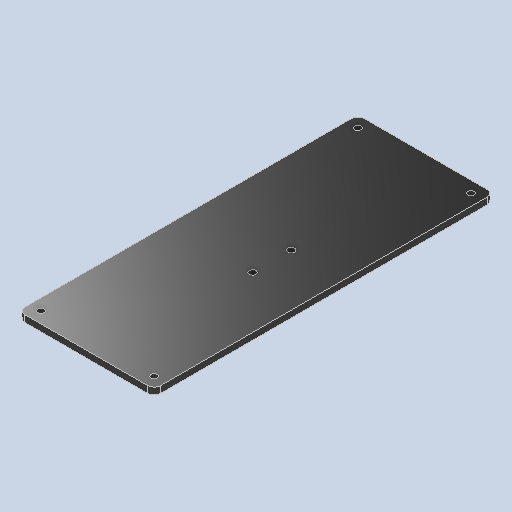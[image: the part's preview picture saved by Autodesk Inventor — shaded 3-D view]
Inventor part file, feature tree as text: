
AUTODESK INVENTOR PART (.ipt)
format: ipt  version: 2023 (Build 270158000, 158)  size: 274,432 bytes
history: native  units: in
note: dims shown in document units (in); Inventor stores cm internally (conversion verified against a paired STEP export)
features: fillet x4, extrude x1, sketch x1
ambient origin geometry x8: Origin, YZ Plane, XZ Plane, XY Plane, X Axis, Y Axis, Z Axis, Center Point
bodies: Solid1 (feature_tree)
feature tree (6):
  extrude  "Extrusion1"  Depth=0.1181in TaperAngle=0.0deg
  fillet  "Fillet1"  Radius=0.1102in
  fillet  "Fillet2"  Radius=0.1102in
  fillet  "Fillet3"  Radius=0.1102in
  fillet  "Fillet4"  Radius=0.1102in
  sketch  "Sketch1"  dims[d0=2.3622in d1=5.9055in d2=0.1969in d3=0.1969in d4=0.1969in d5=0.1969in d6=0.1969in d8=0.1969in d10=0.1102in d11=0.1102in d12=0.7492in d13=0.8681in d14=0.0984in d15=0.0984in d16=0.0984in d17=0.0984in d18=0.1181in d19=0.1181in d20=0.0394in d21=0.1575in d41=0.1181in d42=0.0in d43=0.1102in d44=0.1102in d45=0.1102in d46=0.1102in]
